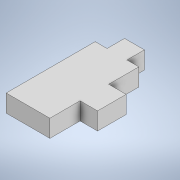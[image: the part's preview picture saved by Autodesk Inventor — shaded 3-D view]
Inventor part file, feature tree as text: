
AUTODESK INVENTOR PART (.ipt)
format: ipt  version: 2020 (Build 240168000, 168)  size: 111,104 bytes
history: native  units: mm
features: extrude x1, sketch x1
ambient origin geometry x8: Origin, YZ Plane, XZ Plane, XY Plane, X Axis, Y Axis, Z Axis, Center Point
bodies: Solide1 (feature_tree)
feature tree (2):
  extrude  "Extrusion1"  Depth=55.0mm
  sketch  "Esquisse1"
